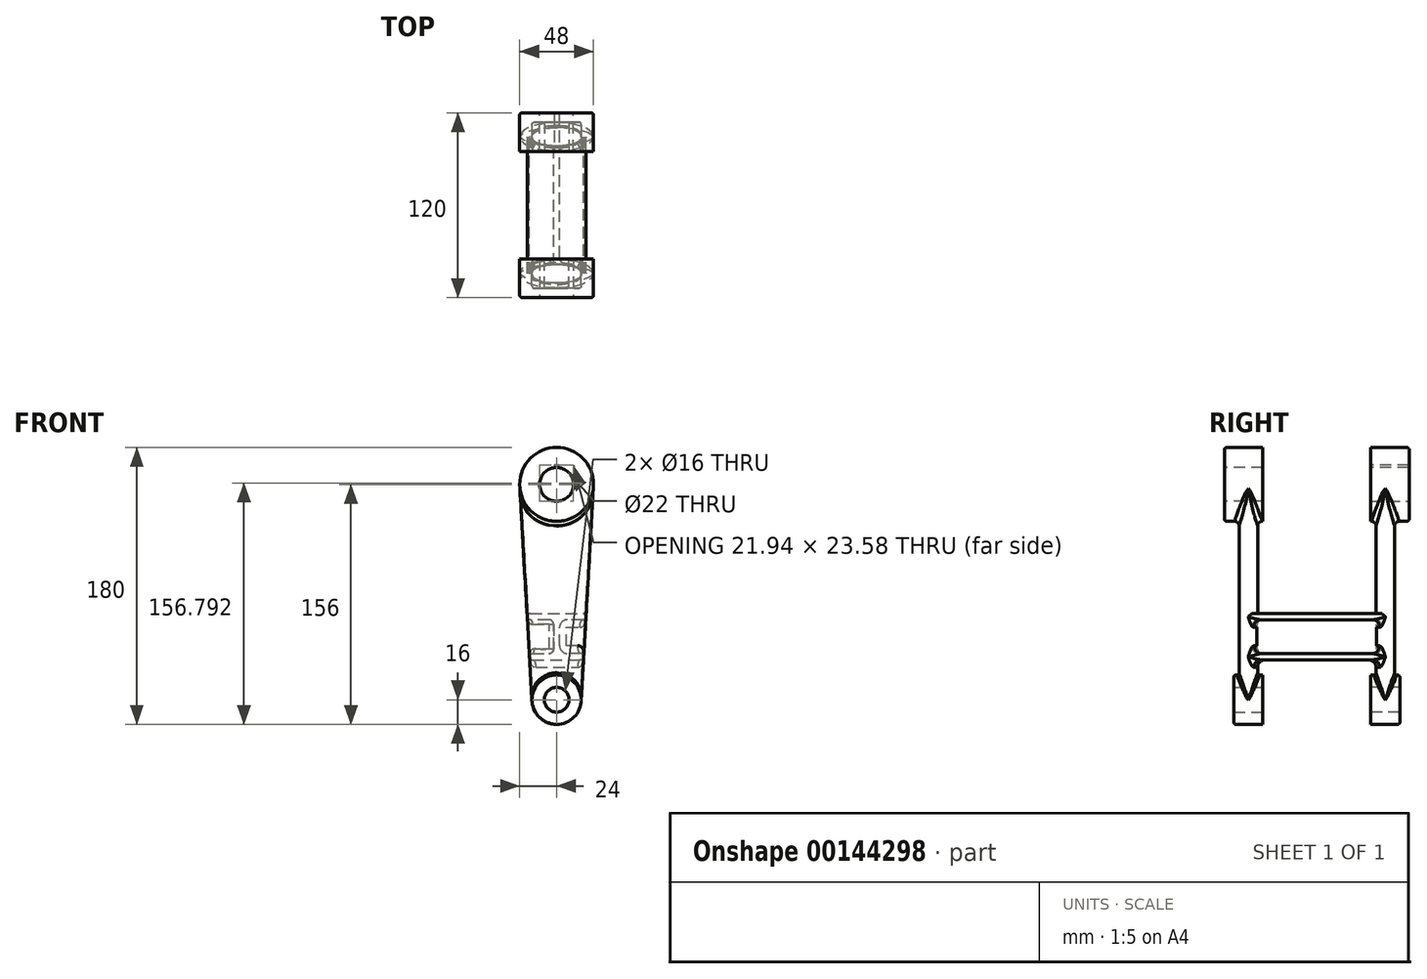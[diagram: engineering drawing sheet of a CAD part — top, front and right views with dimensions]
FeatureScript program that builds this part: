
annotation { "Feature Type Name" : "Feature", "Feature Type Description" : "" }
export const myFeature = defineFeature(function(context is Context, id is Id, definition is map)
    precondition{}
    {
        {
            var Q0;
            Q0=qCreatedBy(makeId("Front.planeOp"),FACE);
            var sketch = newSketch(context, id + "F0", { "sketchPlane" : qUnion([Q0])});
            skCircle(sketch, "E0", {"center": v(0, 140) * mm, "radius": 24 * mm});
            skCircle(sketch, "E1", {"center": v(0, 0) * mm, "radius": 16 * mm});
            skLineSegment(sketch, "E2", {"start": v(-16, 0) * mm, "end": v(-23.96, 138.62) * mm});
            skLineSegment(sketch, "E3", {"start": v(16, 0) * mm, "end": v(23.96, 138.62) * mm});
            skLineSegment(sketch, "E4", {"start": v(-23.96, 138.62) * mm, "end": v(23.96, 138.62) * mm, "construction": true});
            skSolve(sketch);
        }
        {
            var Q0;
            {var subQ0=sQuery(id+"F0.wireOp",EDGE,"E1");var subQ1=makeQuery(id+"F0.imprint","INTERSECT",VERTEX,{"derivedFrom":[subQ0,sQuery(id+"F0.wireOp",EDGE,"E2")]});Q0=makeQuery(id+"F0.imprint","IMPRINT",FACE,{"disambiguationData":[TD([[makeQuery(id+"F0.imprint","IMPRINT",EDGE,{"disambiguationData":[TD([[subQ1,1.0]])],"derivedFrom":subQ0}),1.0]])]});}
            extrude(context, id + "F1", {"entities" : qUnion([Q0]), "depth" : 19 * mm});
        }
        {
            var Q0;
            {var subQ0=sQuery(id+"F0.wireOp",EDGE,"E0");var subQ1=makeQuery(id+"F0.imprint","INTERSECT",VERTEX,{"derivedFrom":[subQ0,sQuery(id+"F0.wireOp",EDGE,"E2")]});Q0=makeQuery(id+"F0.imprint","IMPRINT",FACE,{"disambiguationData":[TD([[makeQuery(id+"F0.imprint","IMPRINT",EDGE,{"disambiguationData":[TD([[subQ1,-1.0]])],"derivedFrom":subQ0}),1.0]])]});}
            extrude(context, id + "F2", {"entities" : qUnion([Q0]), "depth" : 25 * mm});
        }
        {
            var Q0;
            Q0=qCreatedBy(makeId("Top.planeOp"),FACE);
            var sketch = newSketch(context, id + "F3", { "sketchPlane" : qUnion([Q0])});
            skEllipse(sketch, "E5", {"center": v(0, -9.5) * mm, "majorRadius": 16 * mm, "minorRadius": 6 * mm, "majorAxis": v(1, 0)});
            skSolve(sketch);
        }
        {
            var Q0;
            Q0=qCreatedBy(makeId("Top.planeOp"),FACE);
            var Q1;
            Q1=sQuery(id+"F0.wireOp",VERTEX,"E0.center");
            cPlane(context, id + "F4", {"entities" : qUnion([Q0, Q1]), "cplaneType" : CPlaneType.PLANE_POINT, "offset" : 25 * mm, "width" : 150 * mm, "height" : 150 * mm});
        }
        {
            var Q0;
            Q0=qCreatedBy(id+"F4.planeOp",FACE);
            var sketch = newSketch(context, id + "F5", { "sketchPlane" : qUnion([Q0])});
            skLineSegment(sketch, "E6", {"start": v(0, 0) * mm, "end": v(0, -9.5) * mm, "construction": true});
            skEllipse(sketch, "E7", {"center": v(0, -9.5) * mm, "majorRadius": 24 * mm, "minorRadius": 6 * mm, "majorAxis": v(1, 0)});
            skSolve(sketch);
        }
        {
            var Q0;
            Q0=qSketchRegion(id+"F5",true);
            var Q1;
            Q1=qSketchRegion(id+"F3",true);
            loft(context, id + "F6", {"operationType" : NewBodyOperationType.ADD, "sheetProfilesArray" : [{ "sheetProfileEntities" : qUnion([Q0]) }, { "sheetProfileEntities" : qUnion([Q1]) }]});
        }
        {
            var Q0;
            Q0=makeQuery(id+"F2.opExtrude","CAP_FACE",FACE,{"disambiguationData":[OSD([sQuery(id+"F0.wireOp",EDGE,"E0")])],"isStart":false});
            var sketch = newSketch(context, id + "F7", { "sketchPlane" : qUnion([Q0])});
            skCircle(sketch, "E8", {"center": v(0, 140) * mm, "radius": 11 * mm});
            skSolve(sketch);
        }
        {
            var Q0;
            Q0=qSketchRegion(id+"F7",true);
            extrude(context, id + "F8", {"entities" : qUnion([Q0]), "operationType" : NewBodyOperationType.REMOVE, "endBound" : BoundingType.THROUGH_ALL, "oppositeDirection" : true, "depth" : 25 * mm});
        }
        {
            var Q0;
            {var subQ0=sQuery(id+"F0.wireOp",EDGE,"E1");var subQ1=makeQuery(id+"F0.imprint","INTERSECT",VERTEX,{"derivedFrom":[subQ0,sQuery(id+"F0.wireOp",EDGE,"E2")]});Q0=makeQuery(id+"F0.imprint","IMPRINT",FACE,{"disambiguationData":[TD([[makeQuery(id+"F0.imprint","IMPRINT",EDGE,{"disambiguationData":[TD([[subQ1,1.0]])],"derivedFrom":subQ0}),1.0]])]});}
            var sketch = newSketch(context, id + "F9", { "sketchPlane" : qUnion([Q0])});
            skCircle(sketch, "E9", {"center": v(0, 0) * mm, "radius": 8 * mm});
            skSolve(sketch);
        }
        {
            var Q0;
            Q0=qSketchRegion(id+"F9",true);
            extrude(context, id + "F10", {"entities" : qUnion([Q0]), "operationType" : NewBodyOperationType.REMOVE, "endBound" : BoundingType.THROUGH_ALL, "depth" : 25 * mm});
        }
        {
            var Q0;
            Q0=qCreatedBy(makeId("Front.planeOp"),FACE);
            var sketch = newSketch(context, id + "F11", { "sketchPlane" : qUnion([Q0])});
            skCircle(sketch, "E10", {"center": v(0, 0) * mm, "radius": 16 * mm, "construction": true});
            skLineSegment(sketch, "E11", {"start": v(-16, 0) * mm, "end": v(-23.96, 138.62) * mm, "construction": true});
            skLineSegment(sketch, "E12", {"start": v(23.96, 138.62) * mm, "end": v(16.03, 0) * mm, "construction": true});
            skCircle(sketch, "E13", {"center": v(0, 140) * mm, "radius": 24 * mm, "construction": true});
            skLineSegment(sketch, "E14", {"start": v(0, 0) * mm, "end": v(0, 26) * mm, "construction": true});
            skLineSegment(sketch, "E15", {"start": v(0, 26) * mm, "end": v(-17.5, 26) * mm});
            skLineSegment(sketch, "E16", {"start": v(-17.5, 26) * mm, "end": v(-17.72, 30) * mm});
            skLineSegment(sketch, "E17", {"start": v(-17.72, 30) * mm, "end": v(-1.99, 30) * mm});
            skLineSegment(sketch, "E18", {"start": v(-1.99, 30) * mm, "end": v(-1.99, 52) * mm});
            skLineSegment(sketch, "E19", {"start": v(-1.99, 52) * mm, "end": v(-18.99, 52) * mm});
            skLineSegment(sketch, "E20", {"start": v(-18.99, 52) * mm, "end": v(-19.22, 56) * mm});
            skLineSegment(sketch, "E21", {"start": v(-19.22, 56) * mm, "end": v(-2.97, 56) * mm});
            skLineSegment(sketch, "E22", {"start": v(-2.97, 56) * mm, "end": v(19.23, 56) * mm});
            skLineSegment(sketch, "E23", {"start": v(19.23, 56) * mm, "end": v(19, 52) * mm});
            skLineSegment(sketch, "E24", {"start": v(19, 52) * mm, "end": v(2.01, 52) * mm});
            skLineSegment(sketch, "E25", {"start": v(2.01, 52) * mm, "end": v(2.01, 30) * mm});
            skLineSegment(sketch, "E26", {"start": v(2.01, 30) * mm, "end": v(17.74, 30) * mm});
            skLineSegment(sketch, "E27", {"start": v(17.74, 30) * mm, "end": v(17.51, 26) * mm});
            skLineSegment(sketch, "E28", {"start": v(17.51, 26) * mm, "end": v(0, 26) * mm});
            skLineSegment(sketch, "E29", {"start": v(0, 26) * mm, "end": v(17.51, 26) * mm});
            skLineSegment(sketch, "E30", {"start": v(-19.22, 56) * mm, "end": v(19.23, 56) * mm});
            skSolve(sketch);
        }
        {
            var Q0;
            Q0=sQuery(id+"F3.wireOp",VERTEX,"E5.center");
            var Q1;
            Q1=qCreatedBy(makeId("Front.planeOp"),FACE);
            cPlane(context, id + "F12", {"entities" : qUnion([Q0, Q1]), "cplaneType" : CPlaneType.PLANE_POINT, "offset" : 25 * mm, "width" : 150 * mm, "height" : 150 * mm});
        }
        {
            var Q0;
            Q0 = qSketchRegion(id + "F11", true);
            var Q1;
            Q1=qCreatedBy(id+"F12.planeOp",FACE);
            var Q2;
            Q2=makeQuery(id+"F1.opExtrude","SWEPT_BODY",BODY,{"disambiguationData":[OSD([sQuery(id+"F0.wireOp",EDGE,"E1")])]});
            extrude(context, id + "F13", {"entities" : qUnion([Q0]), "operationType" : NewBodyOperationType.ADD, "endBound" : BoundingType.UP_TO_SURFACE, "endBoundEntityFace" : qUnion([Q1]), "endBoundEntityBody" : qUnion([Q2]), "depth" : 25 * mm});
        }
        {
            var Q0;
            Q0 = qSketchRegion(id + "F11", true);
            extrude(context, id + "F14", {"entities" : qUnion([Q0]), "operationType" : NewBodyOperationType.ADD, "oppositeDirection" : true, "depth" : 35 * mm});
        }
        {
            var Q0;
            Q0=makeQuery(id+"F14.opExtrude","CAP_VERTEX",VERTEX,{"disambiguationData":[OSD([sQuery(id+"F11.wireOp",EDGE,"E24"),sQuery(id+"F11.wireOp",EDGE,"E25")])],"isStart":false});
            var Q1;
            Q1=qCreatedBy(makeId("Front.planeOp"),FACE);
            cPlane(context, id + "F15", {"entities" : qUnion([Q0, Q1]), "cplaneType" : CPlaneType.PLANE_POINT, "offset" : 25 * mm, "width" : 150 * mm, "height" : 150 * mm});
        }
        {
            var Q0;
            Q0=makeQuery(id+"F1.opExtrude","SWEPT_BODY",BODY,{"disambiguationData":[OSD([sQuery(id+"F0.wireOp",EDGE,"E1")])]});
            var Q1;
            Q1=qCreatedBy(id+"F15.planeOp",FACE);
            mirror(context, id + "F16", {"operationType" : NewBodyOperationType.ADD, "entities" : qUnion([Q0]), "mirrorPlane" : qUnion([Q1])});
        }
        {
            var Q0;
            {var subQ0=sQuery(id+"F11.wireOp",EDGE,"E30");var subQ1=sQuery(id+"F11.wireOp",EDGE,"E23");var subQ2=makeQuery(id+"F14.boolean.opBoolean","MERGE",EDGE,{"derivedFrom":[makeQuery(id+"F13.opExtrude","SWEPT_EDGE",EDGE,{"disambiguationData":[OSD([subQ1,subQ0])]}),makeQuery(id+"F14.opExtrude","SWEPT_EDGE",EDGE,{"disambiguationData":[OSD([subQ1,subQ0])]})]});Q0=makeQuery(id+"F16.boolean.opBoolean","MERGE",EDGE,{"derivedFrom":[subQ2,makeQuery(id+"F16.opPattern","COPY",EDGE,{"derivedFrom":subQ2,"instanceName":"1"})]});}
            var Q1;
            {var subQ0=sQuery(id+"F11.wireOp",EDGE,"E24");var subQ1=sQuery(id+"F11.wireOp",EDGE,"E23");var subQ2=makeQuery(id+"F14.boolean.opBoolean","MERGE",EDGE,{"derivedFrom":[makeQuery(id+"F13.opExtrude","SWEPT_EDGE",EDGE,{"disambiguationData":[OSD([subQ1,subQ0])]}),makeQuery(id+"F14.opExtrude","SWEPT_EDGE",EDGE,{"disambiguationData":[OSD([subQ1,subQ0])]})]});Q1=makeQuery(id+"F16.boolean.opBoolean","MERGE",EDGE,{"derivedFrom":[subQ2,makeQuery(id+"F16.opPattern","COPY",EDGE,{"derivedFrom":subQ2,"instanceName":"1"})]});}
            var Q2;
            {var subQ0=sQuery(id+"F11.wireOp",EDGE,"E27");var subQ1=sQuery(id+"F11.wireOp",EDGE,"E26");var subQ2=makeQuery(id+"F14.boolean.opBoolean","MERGE",EDGE,{"derivedFrom":[makeQuery(id+"F13.opExtrude","SWEPT_EDGE",EDGE,{"disambiguationData":[OSD([subQ1,subQ0])]}),makeQuery(id+"F14.opExtrude","SWEPT_EDGE",EDGE,{"disambiguationData":[OSD([subQ1,subQ0])]})]});Q2=makeQuery(id+"F16.boolean.opBoolean","MERGE",EDGE,{"derivedFrom":[subQ2,makeQuery(id+"F16.opPattern","COPY",EDGE,{"derivedFrom":subQ2,"instanceName":"1"})]});}
            var Q3;
            {var subQ0=sQuery(id+"F11.wireOp",EDGE,"E29");var subQ1=sQuery(id+"F11.wireOp",EDGE,"E27");var subQ2=makeQuery(id+"F14.boolean.opBoolean","MERGE",EDGE,{"derivedFrom":[makeQuery(id+"F13.opExtrude","SWEPT_EDGE",EDGE,{"disambiguationData":[OSD([subQ1,subQ0])]}),makeQuery(id+"F14.opExtrude","SWEPT_EDGE",EDGE,{"disambiguationData":[OSD([subQ1,subQ0])]})]});Q3=makeQuery(id+"F16.boolean.opBoolean","MERGE",EDGE,{"derivedFrom":[subQ2,makeQuery(id+"F16.opPattern","COPY",EDGE,{"derivedFrom":subQ2,"instanceName":"1"})]});}
            var Q4;
            {var subQ0=sQuery(id+"F11.wireOp",EDGE,"E30");var subQ1=sQuery(id+"F11.wireOp",EDGE,"E20");var subQ2=makeQuery(id+"F14.boolean.opBoolean","MERGE",EDGE,{"derivedFrom":[makeQuery(id+"F13.opExtrude","SWEPT_EDGE",EDGE,{"disambiguationData":[OSD([subQ1,subQ0])]}),makeQuery(id+"F14.opExtrude","SWEPT_EDGE",EDGE,{"disambiguationData":[OSD([subQ1,subQ0])]})]});Q4=makeQuery(id+"F16.boolean.opBoolean","MERGE",EDGE,{"derivedFrom":[subQ2,makeQuery(id+"F16.opPattern","COPY",EDGE,{"derivedFrom":subQ2,"instanceName":"1"})]});}
            var Q5;
            {var subQ0=sQuery(id+"F11.wireOp",EDGE,"E20");var subQ1=sQuery(id+"F11.wireOp",EDGE,"E19");var subQ2=makeQuery(id+"F14.boolean.opBoolean","MERGE",EDGE,{"derivedFrom":[makeQuery(id+"F13.opExtrude","SWEPT_EDGE",EDGE,{"disambiguationData":[OSD([subQ1,subQ0])]}),makeQuery(id+"F14.opExtrude","SWEPT_EDGE",EDGE,{"disambiguationData":[OSD([subQ1,subQ0])]})]});Q5=makeQuery(id+"F16.boolean.opBoolean","MERGE",EDGE,{"derivedFrom":[subQ2,makeQuery(id+"F16.opPattern","COPY",EDGE,{"derivedFrom":subQ2,"instanceName":"1"})]});}
            var Q6;
            {var subQ0=sQuery(id+"F11.wireOp",EDGE,"E17");var subQ1=sQuery(id+"F11.wireOp",EDGE,"E16");var subQ2=makeQuery(id+"F14.boolean.opBoolean","MERGE",EDGE,{"derivedFrom":[makeQuery(id+"F13.opExtrude","SWEPT_EDGE",EDGE,{"disambiguationData":[OSD([subQ1,subQ0])]}),makeQuery(id+"F14.opExtrude","SWEPT_EDGE",EDGE,{"disambiguationData":[OSD([subQ1,subQ0])]})]});Q6=makeQuery(id+"F16.boolean.opBoolean","MERGE",EDGE,{"derivedFrom":[subQ2,makeQuery(id+"F16.opPattern","COPY",EDGE,{"derivedFrom":subQ2,"instanceName":"1"})]});}
            var Q7;
            {var subQ0=sQuery(id+"F11.wireOp",EDGE,"E16");var subQ1=sQuery(id+"F11.wireOp",EDGE,"E15");var subQ2=makeQuery(id+"F14.boolean.opBoolean","MERGE",EDGE,{"derivedFrom":[makeQuery(id+"F13.opExtrude","SWEPT_EDGE",EDGE,{"disambiguationData":[OSD([subQ1,subQ0])]}),makeQuery(id+"F14.opExtrude","SWEPT_EDGE",EDGE,{"disambiguationData":[OSD([subQ1,subQ0])]})]});Q7=makeQuery(id+"F16.boolean.opBoolean","MERGE",EDGE,{"derivedFrom":[subQ2,makeQuery(id+"F16.opPattern","COPY",EDGE,{"derivedFrom":subQ2,"instanceName":"1"})]});}
            fillet(context, id + "F17", {"entities" : qUnion([Q0, Q1, Q2, Q3, Q4, Q5, Q6, Q7]), "radius" : 2 * mm, "tangentPropagation" : true, "allowEdgeOverflow" : false});
        }
        {
            var Q0;
            Q0=makeQuery(id+"F6.boolean.opBoolean","INTERSECT",EDGE,{"derivedFrom":[makeQuery(id+"F2.opExtrude","SWEPT_FACE",FACE,{"disambiguationData":[OSD([sQuery(id+"F0.wireOp",EDGE,"E0")])]}),makeQuery(id+"F6.opLoft","SWEPT_FACE",FACE,{"disambiguationData":[OSD([sQuery(id+"F3.wireOp",EDGE,"E5"),sQuery(id+"F5.wireOp",EDGE,"E7")])]})]});
            var Q1;
            Q1=makeQuery(id+"F16.opPattern","COPY",EDGE,{"derivedFrom":makeQuery(id+"F6.boolean.opBoolean","INTERSECT",EDGE,{"derivedFrom":[makeQuery(id+"F2.opExtrude","SWEPT_FACE",FACE,{"disambiguationData":[OSD([sQuery(id+"F0.wireOp",EDGE,"E0")])]}),makeQuery(id+"F6.opLoft","SWEPT_FACE",FACE,{"disambiguationData":[OSD([sQuery(id+"F3.wireOp",EDGE,"E5"),sQuery(id+"F5.wireOp",EDGE,"E7")])]})]}),"instanceName":"1"});
            fillet(context, id + "F18", {"entities" : qUnion([Q0, Q1]), "radius" : 3 * mm, "tangentPropagation" : true, "allowEdgeOverflow" : false});
        }
        {
            var Q0;
            Q0=makeQuery(id+"F13.boolean.opBoolean","INTERSECT",EDGE,{"derivedFrom":[makeQuery(id+"F6.opLoft","SWEPT_FACE",FACE,{"disambiguationData":[OSD([sQuery(id+"F3.wireOp",EDGE,"E5"),sQuery(id+"F5.wireOp",EDGE,"E7")])]}),makeQuery(id+"F13.opExtrude","SWEPT_FACE",FACE,{"disambiguationData":[OSD([sQuery(id+"F11.wireOp",EDGE,"E26")])]})]});
            var Q1;
            Q1=makeQuery(id+"F13.boolean.opBoolean","INTERSECT",EDGE,{"derivedFrom":[makeQuery(id+"F6.opLoft","SWEPT_FACE",FACE,{"disambiguationData":[OSD([sQuery(id+"F3.wireOp",EDGE,"E5"),sQuery(id+"F5.wireOp",EDGE,"E7")])]}),makeQuery(id+"F13.opExtrude","SWEPT_FACE",FACE,{"disambiguationData":[OSD([sQuery(id+"F11.wireOp",EDGE,"E25")])]})]});
            var Q2;
            Q2=makeQuery(id+"F16.opPattern","COPY",EDGE,{"derivedFrom":makeQuery(id+"F13.boolean.opBoolean","INTERSECT",EDGE,{"derivedFrom":[makeQuery(id+"F6.opLoft","SWEPT_FACE",FACE,{"disambiguationData":[OSD([sQuery(id+"F3.wireOp",EDGE,"E5"),sQuery(id+"F5.wireOp",EDGE,"E7")])]}),makeQuery(id+"F13.opExtrude","SWEPT_FACE",FACE,{"disambiguationData":[OSD([sQuery(id+"F11.wireOp",EDGE,"E26")])]})]}),"instanceName":"1"});
            var Q3;
            {var subQ0=sQuery(id+"F11.wireOp",EDGE,"E26");var subQ1=sQuery(id+"F11.wireOp",EDGE,"E25");var subQ2=makeQuery(id+"F14.boolean.opBoolean","MERGE",EDGE,{"derivedFrom":[makeQuery(id+"F13.opExtrude","SWEPT_EDGE",EDGE,{"disambiguationData":[OSD([subQ1,subQ0])]}),makeQuery(id+"F14.opExtrude","SWEPT_EDGE",EDGE,{"disambiguationData":[OSD([subQ1,subQ0])]})]});Q3=makeQuery(id+"F16.boolean.opBoolean","MERGE",EDGE,{"derivedFrom":[subQ2,makeQuery(id+"F16.opPattern","COPY",EDGE,{"derivedFrom":subQ2,"instanceName":"1"})]});}
            var Q4;
            Q4=makeQuery(id+"F16.opPattern","COPY",EDGE,{"derivedFrom":makeQuery(id+"F13.boolean.opBoolean","INTERSECT",EDGE,{"derivedFrom":[makeQuery(id+"F6.opLoft","SWEPT_FACE",FACE,{"disambiguationData":[OSD([sQuery(id+"F3.wireOp",EDGE,"E5"),sQuery(id+"F5.wireOp",EDGE,"E7")])]}),makeQuery(id+"F13.opExtrude","SWEPT_FACE",FACE,{"disambiguationData":[OSD([sQuery(id+"F11.wireOp",EDGE,"E25")])]})]}),"instanceName":"1"});
            var Q5;
            Q5=makeQuery(id+"F16.opPattern","COPY",EDGE,{"derivedFrom":makeQuery(id+"F13.boolean.opBoolean","INTERSECT",EDGE,{"derivedFrom":[makeQuery(id+"F6.opLoft","SWEPT_FACE",FACE,{"disambiguationData":[OSD([sQuery(id+"F3.wireOp",EDGE,"E5"),sQuery(id+"F5.wireOp",EDGE,"E7")])]}),makeQuery(id+"F13.opExtrude","SWEPT_FACE",FACE,{"disambiguationData":[OSD([sQuery(id+"F11.wireOp",EDGE,"E24")])]})]}),"instanceName":"1"});
            var Q6;
            {var subQ0=sQuery(id+"F11.wireOp",EDGE,"E25");var subQ1=sQuery(id+"F11.wireOp",EDGE,"E24");var subQ2=makeQuery(id+"F14.boolean.opBoolean","MERGE",EDGE,{"derivedFrom":[makeQuery(id+"F13.opExtrude","SWEPT_EDGE",EDGE,{"disambiguationData":[OSD([subQ1,subQ0])]}),makeQuery(id+"F14.opExtrude","SWEPT_EDGE",EDGE,{"disambiguationData":[OSD([subQ1,subQ0])]})]});Q6=makeQuery(id+"F16.boolean.opBoolean","MERGE",EDGE,{"derivedFrom":[subQ2,makeQuery(id+"F16.opPattern","COPY",EDGE,{"derivedFrom":subQ2,"instanceName":"1"})]});}
            var Q7;
            Q7=makeQuery(id+"F13.boolean.opBoolean","INTERSECT",EDGE,{"derivedFrom":[makeQuery(id+"F6.opLoft","SWEPT_FACE",FACE,{"disambiguationData":[OSD([sQuery(id+"F3.wireOp",EDGE,"E5"),sQuery(id+"F5.wireOp",EDGE,"E7")])]}),makeQuery(id+"F13.opExtrude","SWEPT_FACE",FACE,{"disambiguationData":[OSD([sQuery(id+"F11.wireOp",EDGE,"E24")])]})]});
            var Q8;
            Q8=makeQuery(id+"F13.boolean.opBoolean","INTERSECT",EDGE,{"derivedFrom":[makeQuery(id+"F6.opLoft","SWEPT_FACE",FACE,{"disambiguationData":[OSD([sQuery(id+"F3.wireOp",EDGE,"E5"),sQuery(id+"F5.wireOp",EDGE,"E7")])]}),makeQuery(id+"F13.opExtrude","SWEPT_FACE",FACE,{"disambiguationData":[OSD([sQuery(id+"F11.wireOp",EDGE,"E15"),sQuery(id+"F11.wireOp",EDGE,"E29")])]})]});
            var Q9;
            Q9=makeQuery(id+"F16.opPattern","COPY",EDGE,{"derivedFrom":makeQuery(id+"F13.boolean.opBoolean","INTERSECT",EDGE,{"derivedFrom":[makeQuery(id+"F6.opLoft","SWEPT_FACE",FACE,{"disambiguationData":[OSD([sQuery(id+"F3.wireOp",EDGE,"E5"),sQuery(id+"F5.wireOp",EDGE,"E7")])]}),makeQuery(id+"F13.opExtrude","SWEPT_FACE",FACE,{"disambiguationData":[OSD([sQuery(id+"F11.wireOp",EDGE,"E15"),sQuery(id+"F11.wireOp",EDGE,"E29")])]})]}),"instanceName":"1"});
            var Q10;
            Q10=makeQuery(id+"F16.opPattern","COPY",EDGE,{"derivedFrom":makeQuery(id+"F13.boolean.opBoolean","INTERSECT",EDGE,{"derivedFrom":[makeQuery(id+"F6.opLoft","SWEPT_FACE",FACE,{"disambiguationData":[OSD([sQuery(id+"F3.wireOp",EDGE,"E5"),sQuery(id+"F5.wireOp",EDGE,"E7")])]}),makeQuery(id+"F13.opExtrude","SWEPT_FACE",FACE,{"disambiguationData":[OSD([sQuery(id+"F11.wireOp",EDGE,"E30")])]})]}),"instanceName":"1"});
            var Q11;
            Q11=makeQuery(id+"F13.boolean.opBoolean","INTERSECT",EDGE,{"derivedFrom":[makeQuery(id+"F6.opLoft","SWEPT_FACE",FACE,{"disambiguationData":[OSD([sQuery(id+"F3.wireOp",EDGE,"E5"),sQuery(id+"F5.wireOp",EDGE,"E7")])]}),makeQuery(id+"F13.opExtrude","SWEPT_FACE",FACE,{"disambiguationData":[OSD([sQuery(id+"F11.wireOp",EDGE,"E30")])]})]});
            fillet(context, id + "F19", {"entities" : qUnion([Q0, Q1, Q2, Q3, Q4, Q5, Q6, Q7, Q8, Q9, Q10, Q11]), "radius" : 5 * mm, "tangentPropagation" : true, "allowEdgeOverflow" : false});
        }
        {
            var Q0;
            Q0=makeQuery(id+"F16.opPattern","COPY",EDGE,{"derivedFrom":makeQuery(id+"F6.boolean.opBoolean","INTERSECT",EDGE,{"derivedFrom":[makeQuery(id+"F1.opExtrude","SWEPT_FACE",FACE,{"disambiguationData":[OSD([sQuery(id+"F0.wireOp",EDGE,"E1")])]}),makeQuery(id+"F6.opLoft","SWEPT_FACE",FACE,{"disambiguationData":[OSD([sQuery(id+"F3.wireOp",EDGE,"E5"),sQuery(id+"F5.wireOp",EDGE,"E7")])]})]}),"instanceName":"1"});
            var Q1;
            Q1=makeQuery(id+"F6.boolean.opBoolean","INTERSECT",EDGE,{"derivedFrom":[makeQuery(id+"F1.opExtrude","SWEPT_FACE",FACE,{"disambiguationData":[OSD([sQuery(id+"F0.wireOp",EDGE,"E1")])]}),makeQuery(id+"F6.opLoft","SWEPT_FACE",FACE,{"disambiguationData":[OSD([sQuery(id+"F3.wireOp",EDGE,"E5"),sQuery(id+"F5.wireOp",EDGE,"E7")])]})]});
            fillet(context, id + "F20", {"entities" : qUnion([Q0, Q1]), "radius" : 1.5 * mm, "tangentPropagation" : true, "allowEdgeOverflow" : false});
        }
        {
            var Q0;
            Q0=makeQuery(id+"F16.opPattern","COPY",EDGE,{"derivedFrom":makeQuery(id+"F13.boolean.opBoolean","INTERSECT",EDGE,{"derivedFrom":[makeQuery(id+"F6.opLoft","SWEPT_FACE",FACE,{"disambiguationData":[OSD([sQuery(id+"F3.wireOp",EDGE,"E5"),sQuery(id+"F5.wireOp",EDGE,"E7")])]}),makeQuery(id+"F13.opExtrude","SWEPT_FACE",FACE,{"disambiguationData":[OSD([sQuery(id+"F11.wireOp",EDGE,"E19")])]})]}),"instanceName":"1"});
            var Q1;
            Q1=makeQuery(id+"F16.opPattern","COPY",EDGE,{"derivedFrom":makeQuery(id+"F13.boolean.opBoolean","INTERSECT",EDGE,{"derivedFrom":[makeQuery(id+"F6.opLoft","SWEPT_FACE",FACE,{"disambiguationData":[OSD([sQuery(id+"F3.wireOp",EDGE,"E5"),sQuery(id+"F5.wireOp",EDGE,"E7")])]}),makeQuery(id+"F13.opExtrude","SWEPT_FACE",FACE,{"disambiguationData":[OSD([sQuery(id+"F11.wireOp",EDGE,"E18")])]})]}),"instanceName":"1"});
            var Q2;
            {var subQ0=sQuery(id+"F11.wireOp",EDGE,"E19");var subQ1=sQuery(id+"F11.wireOp",EDGE,"E18");var subQ2=makeQuery(id+"F14.boolean.opBoolean","MERGE",EDGE,{"derivedFrom":[makeQuery(id+"F13.opExtrude","SWEPT_EDGE",EDGE,{"disambiguationData":[OSD([subQ1,subQ0])]}),makeQuery(id+"F14.opExtrude","SWEPT_EDGE",EDGE,{"disambiguationData":[OSD([subQ1,subQ0])]})]});Q2=makeQuery(id+"F16.boolean.opBoolean","MERGE",EDGE,{"derivedFrom":[subQ2,makeQuery(id+"F16.opPattern","COPY",EDGE,{"derivedFrom":subQ2,"instanceName":"1"})]});}
            var Q3;
            Q3=makeQuery(id+"F16.opPattern","COPY",EDGE,{"derivedFrom":makeQuery(id+"F13.boolean.opBoolean","INTERSECT",EDGE,{"derivedFrom":[makeQuery(id+"F6.opLoft","SWEPT_FACE",FACE,{"disambiguationData":[OSD([sQuery(id+"F3.wireOp",EDGE,"E5"),sQuery(id+"F5.wireOp",EDGE,"E7")])]}),makeQuery(id+"F13.opExtrude","SWEPT_FACE",FACE,{"disambiguationData":[OSD([sQuery(id+"F11.wireOp",EDGE,"E17")])]})]}),"instanceName":"1"});
            var Q4;
            {var subQ0=sQuery(id+"F11.wireOp",EDGE,"E18");var subQ1=sQuery(id+"F11.wireOp",EDGE,"E17");var subQ2=makeQuery(id+"F14.boolean.opBoolean","MERGE",EDGE,{"derivedFrom":[makeQuery(id+"F13.opExtrude","SWEPT_EDGE",EDGE,{"disambiguationData":[OSD([subQ1,subQ0])]}),makeQuery(id+"F14.opExtrude","SWEPT_EDGE",EDGE,{"disambiguationData":[OSD([subQ1,subQ0])]})]});Q4=makeQuery(id+"F16.boolean.opBoolean","MERGE",EDGE,{"derivedFrom":[subQ2,makeQuery(id+"F16.opPattern","COPY",EDGE,{"derivedFrom":subQ2,"instanceName":"1"})]});}
            var Q5;
            Q5=makeQuery(id+"F13.boolean.opBoolean","INTERSECT",EDGE,{"derivedFrom":[makeQuery(id+"F6.opLoft","SWEPT_FACE",FACE,{"disambiguationData":[OSD([sQuery(id+"F3.wireOp",EDGE,"E5"),sQuery(id+"F5.wireOp",EDGE,"E7")])]}),makeQuery(id+"F13.opExtrude","SWEPT_FACE",FACE,{"disambiguationData":[OSD([sQuery(id+"F11.wireOp",EDGE,"E17")])]})]});
            var Q6;
            Q6=makeQuery(id+"F13.boolean.opBoolean","INTERSECT",EDGE,{"derivedFrom":[makeQuery(id+"F6.opLoft","SWEPT_FACE",FACE,{"disambiguationData":[OSD([sQuery(id+"F3.wireOp",EDGE,"E5"),sQuery(id+"F5.wireOp",EDGE,"E7")])]}),makeQuery(id+"F13.opExtrude","SWEPT_FACE",FACE,{"disambiguationData":[OSD([sQuery(id+"F11.wireOp",EDGE,"E19")])]})]});
            fillet(context, id + "F21", {"entities" : qUnion([Q0, Q1, Q2, Q3, Q4, Q5, Q6]), "radius" : 3 * mm, "tangentPropagation" : true, "allowEdgeOverflow" : false});
        }
        {
            var Q0;
            Q0=makeQuery(id+"F2.opExtrude","CAP_EDGE",EDGE,{"disambiguationData":[OSD([sQuery(id+"F0.wireOp",EDGE,"E0")])],"isStart":false});
            var Q1;
            Q1=makeQuery(id+"F16.opPattern","COPY",EDGE,{"derivedFrom":makeQuery(id+"F2.opExtrude","CAP_EDGE",EDGE,{"disambiguationData":[OSD([sQuery(id+"F0.wireOp",EDGE,"E0")])],"isStart":false}),"instanceName":"1"});
            var Q2;
            Q2=makeQuery(id+"F16.opPattern","COPY",EDGE,{"derivedFrom":makeQuery(id+"F1.opExtrude","CAP_EDGE",EDGE,{"disambiguationData":[OSD([sQuery(id+"F0.wireOp",EDGE,"E1")])],"isStart":false}),"instanceName":"1"});
            var Q3;
            Q3=makeQuery(id+"F1.opExtrude","CAP_EDGE",EDGE,{"disambiguationData":[OSD([sQuery(id+"F0.wireOp",EDGE,"E1")])],"isStart":false});
            fillet(context, id + "F22", {"entities" : qUnion([Q0, Q1, Q2, Q3]), "radius" : 1.5 * mm, "tangentPropagation" : true, "allowEdgeOverflow" : false});
        }
        {
            var Q0;
            Q0=makeQuery(id+"F16.opPattern","COPY",FACE,{"derivedFrom":makeQuery(id+"F2.opExtrude","CAP_FACE",FACE,{"disambiguationData":[OSD([sQuery(id+"F0.wireOp",EDGE,"E0")])],"isStart":true}),"instanceName":"1"});
            var sketch = newSketch(context, id + "F23", { "sketchPlane" : qUnion([Q0])});
            skLineSegment(sketch, "E31", {"start": v(0, 150.88) * mm, "end": v(0, 164) * mm, "construction": true});
            skLineSegment(sketch, "E32.bottom", {"start": v(0, 150.88) * mm, "end": v(-1.6, 150.88) * mm, "construction": true});
            skLineSegment(sketch, "E32.top", {"start": v(0, 146.88) * mm, "end": v(-1.6, 146.88) * mm, "construction": true});
            skLineSegment(sketch, "E32.left", {"start": v(0, 150.88) * mm, "end": v(0, 146.88) * mm, "construction": true});
            skLineSegment(sketch, "E32.right", {"start": v(-1.6, 150.88) * mm, "end": v(-1.6, 146.88) * mm, "construction": true});
            skPoint(sketch, "E33.oppositeSnap0", {"position": v(-0.8, 146.88) * mm});
            skLineSegment(sketch, "E33.bottom", {"start": v(0, 150.88) * mm, "end": v(1.6, 150.88) * mm, "construction": true});
            skLineSegment(sketch, "E33.top", {"start": v(0, 146.88) * mm, "end": v(1.6, 146.88) * mm, "construction": true});
            skLineSegment(sketch, "E33.right", {"start": v(1.6, 150.88) * mm, "end": v(1.6, 146.88) * mm, "construction": true});
            skLineSegment(sketch, "E34.bottom", {"start": v(-1.6, 150.88) * mm, "end": v(1.6, 150.88) * mm});
            skLineSegment(sketch, "E34.top", {"start": v(-1.6, 152.58) * mm, "end": v(1.6, 152.58) * mm});
            skLineSegment(sketch, "E34.left", {"start": v(-1.6, 150.88) * mm, "end": v(-1.6, 152.58) * mm});
            skLineSegment(sketch, "E34.right", {"start": v(1.6, 150.88) * mm, "end": v(1.6, 152.58) * mm});
            skSolve(sketch);
        }
        {
            var Q0;
            Q0=makeQuery(id+"F23.imprint","IMPRINT",FACE,{"disambiguationData":[TD([[makeQuery(id+"F23.imprint","IMPRINT",EDGE,{"derivedFrom":sQuery(id+"F23.wireOp",EDGE,"E34.top")}),-1.0]])]});
            extrude(context, id + "F24", {"entities" : qUnion([Q0]), "operationType" : NewBodyOperationType.REMOVE, "endBound" : BoundingType.THROUGH_ALL, "oppositeDirection" : true, "depth" : 25 * mm});
        }
    });
